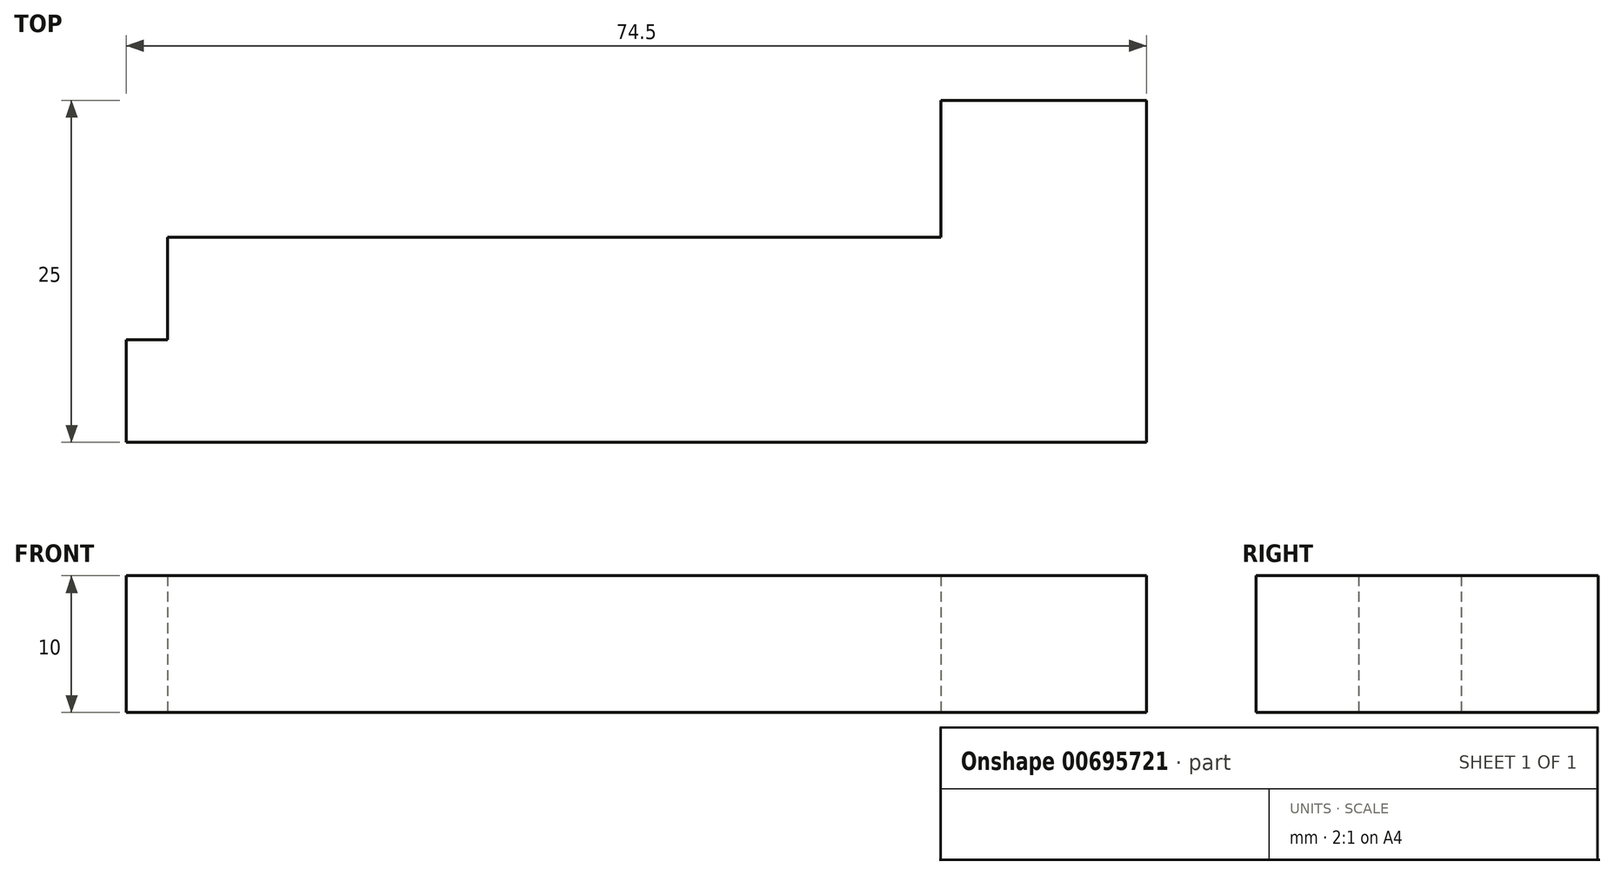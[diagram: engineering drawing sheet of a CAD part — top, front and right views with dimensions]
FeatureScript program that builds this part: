
annotation { "Feature Type Name" : "Feature", "Feature Type Description" : "" }
export const myFeature = defineFeature(function(context is Context, id is Id, definition is map)
    precondition{}
    {
        {
            var Q0;
            Q0=qCreatedBy(makeId("Top.planeOp"),FACE);
            var sketch = newSketch(context, id + "F0", { "sketchPlane" : qUnion([Q0])});
            skLineSegment(sketch, "E0", {"start": v(0, 0) * mm, "end": v(58, 0) * mm});
            skLineSegment(sketch, "E1", {"start": v(58, 0) * mm, "end": v(58, 10) * mm});
            skLineSegment(sketch, "E2", {"start": v(58, 10) * mm, "end": v(73, 10) * mm});
            skLineSegment(sketch, "E3", {"start": v(73, 10) * mm, "end": v(73, -15) * mm});
            skLineSegment(sketch, "E4", {"start": v(73, -15) * mm, "end": v(0, -15) * mm});
            skLineSegment(sketch, "E5", {"start": v(0, -15) * mm, "end": v(0, 0) * mm});
            skSolve(sketch);
        }
        {
            var Q0;
            Q0 = qSketchRegion(id + "F0", true);
            extrude(context, id + "F1", {"entities" : qUnion([Q0]), "depth" : 10 * mm, "offsetDistance" : 25 * mm});
        }
        {
            var Q0;
            Q0=makeQuery(id+"F1.opExtrude","SWEPT_FACE",FACE,{"disambiguationData":[OSD([sQuery(id+"F0.wireOp",EDGE,"E5")])]});
            var sketch = newSketch(context, id + "F2", { "sketchPlane" : qUnion([Q0])});
            skLineSegment(sketch, "E6.bottom", {"start": v(0, 10) * mm, "end": v(7.5, 10) * mm});
            skLineSegment(sketch, "E6.top", {"start": v(0, 0) * mm, "end": v(7.5, 0) * mm});
            skLineSegment(sketch, "E6.left", {"start": v(0, 10) * mm, "end": v(0, 0) * mm});
            skLineSegment(sketch, "E6.right", {"start": v(7.5, 10) * mm, "end": v(7.5, 0) * mm});
            skSolve(sketch);
        }
        {
            var Q0;
            Q0 = qSketchRegion(id + "F2", true);
            extrude(context, id + "F3", {"entities" : qUnion([Q0]), "operationType" : NewBodyOperationType.REMOVE, "oppositeDirection" : true, "depth" : 1.5 * mm, "offsetDistance" : 25 * mm});
        }
        {
            var Q0;
            Q0=makeQuery(id+"F1.opExtrude","SWEPT_FACE",FACE,{"disambiguationData":[OSD([sQuery(id+"F0.wireOp",EDGE,"E5")])]});
            var sketch = newSketch(context, id + "F4", { "sketchPlane" : qUnion([Q0])});
            skLineSegment(sketch, "E7.bottom", {"start": v(15, 10) * mm, "end": v(7.5, 10) * mm});
            skLineSegment(sketch, "E7.top", {"start": v(15, 0) * mm, "end": v(7.5, 0) * mm});
            skLineSegment(sketch, "E7.left", {"start": v(15, 10) * mm, "end": v(15, 0) * mm});
            skLineSegment(sketch, "E7.right", {"start": v(7.5, 10) * mm, "end": v(7.5, 0) * mm});
            skSolve(sketch);
        }
        {
            var Q0;
            Q0 = qSketchRegion(id + "F4", true);
            extrude(context, id + "F5", {"entities" : qUnion([Q0]), "operationType" : NewBodyOperationType.ADD, "depth" : 1.5 * mm, "offsetDistance" : 25 * mm});
        }
    });
